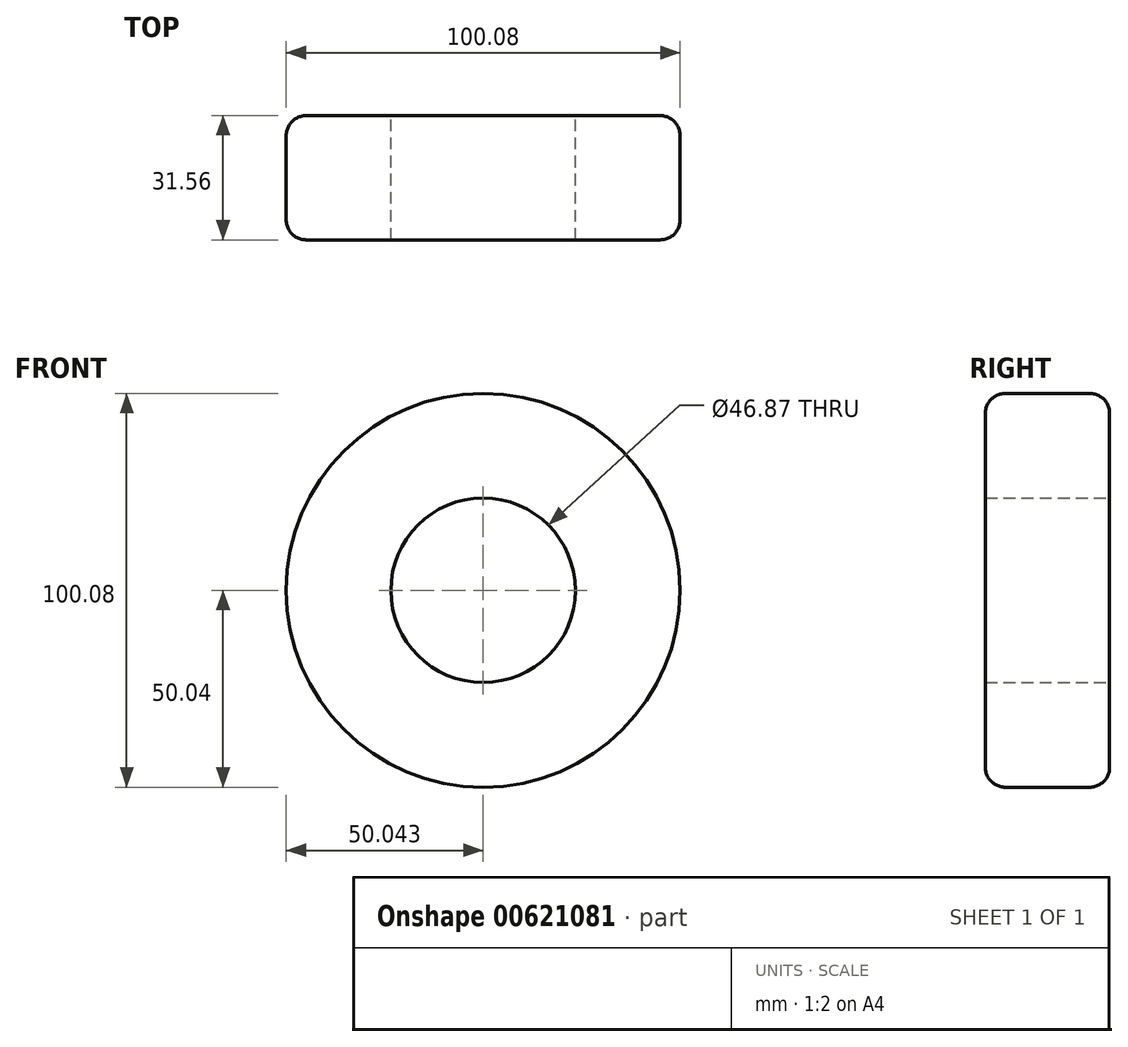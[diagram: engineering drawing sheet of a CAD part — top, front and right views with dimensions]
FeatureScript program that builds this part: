
annotation { "Feature Type Name" : "Feature", "Feature Type Description" : "" }
export const myFeature = defineFeature(function(context is Context, id is Id, definition is map)
    precondition{}
    {
        {
            var Q0;
            Q0=qCreatedBy(makeId("Top.planeOp"),FACE);
            var sketch = newSketch(context, id + "F0", { "sketchPlane" : qUnion([Q0])});
            skLineSegment(sketch, "E0.bottom", {"start": v(0, 0) * mm, "end": v(-26.6, 0) * mm});
            skLineSegment(sketch, "E0.top", {"start": v(0, -31.56) * mm, "end": v(-26.6, -31.56) * mm});
            skLineSegment(sketch, "E0.left", {"start": v(0, 0) * mm, "end": v(0, -31.56) * mm});
            skLineSegment(sketch, "E0.right", {"start": v(-26.6, 0) * mm, "end": v(-26.6, -31.56) * mm});
            skSolve(sketch);
        }
        {
            var Q0;
            Q0=qCreatedBy(makeId("Top.planeOp"),FACE);
            var sketch = newSketch(context, id + "F1", { "sketchPlane" : qUnion([Q0])});
            skLineSegment(sketch, "E1", {"start": v(23.43, 0) * mm, "end": v(23.43, -36.78) * mm});
            skSolve(sketch);
        }
        {
            var Q0;
            Q0=makeQuery(id+"F0.imprint","IMPRINT",FACE,{"disambiguationData":[TD([[makeQuery(id+"F0.imprint","IMPRINT",EDGE,{"derivedFrom":sQuery(id+"F0.wireOp",EDGE,"E0.bottom")}),1.0]])]});
            var Q1;
            Q1=sQuery(id+"F1.wireOp",EDGE,"E1");
            revolve(context, id + "F2", {"entities" : qUnion([Q0]), "axis" : qUnion([Q1]), "revolveType" : RevolveType.FULL});
        }
        {
            var Q0;
            Q0=makeQuery(id+"F2.opRevolve","SWEPT_EDGE",EDGE,{"disambiguationData":[OSD([sQuery(id+"F0.wireOp",EDGE,"E0.bottom"),sQuery(id+"F0.wireOp",EDGE,"E0.right")])]});
            fillet(context, id + "F3", {"entities" : qUnion([Q0]), "radius" : 5.08 * mm, "tangentPropagation" : true, "allowEdgeOverflow" : false});
        }
        {
            var Q0;
            Q0=makeQuery(id+"F2.opRevolve","SWEPT_EDGE",EDGE,{"disambiguationData":[OSD([sQuery(id+"F0.wireOp",EDGE,"E0.top"),sQuery(id+"F0.wireOp",EDGE,"E0.right")])]});
            fillet(context, id + "F4", {"entities" : qUnion([Q0]), "radius" : 5.08 * mm, "tangentPropagation" : true, "allowEdgeOverflow" : false});
        }
    });
